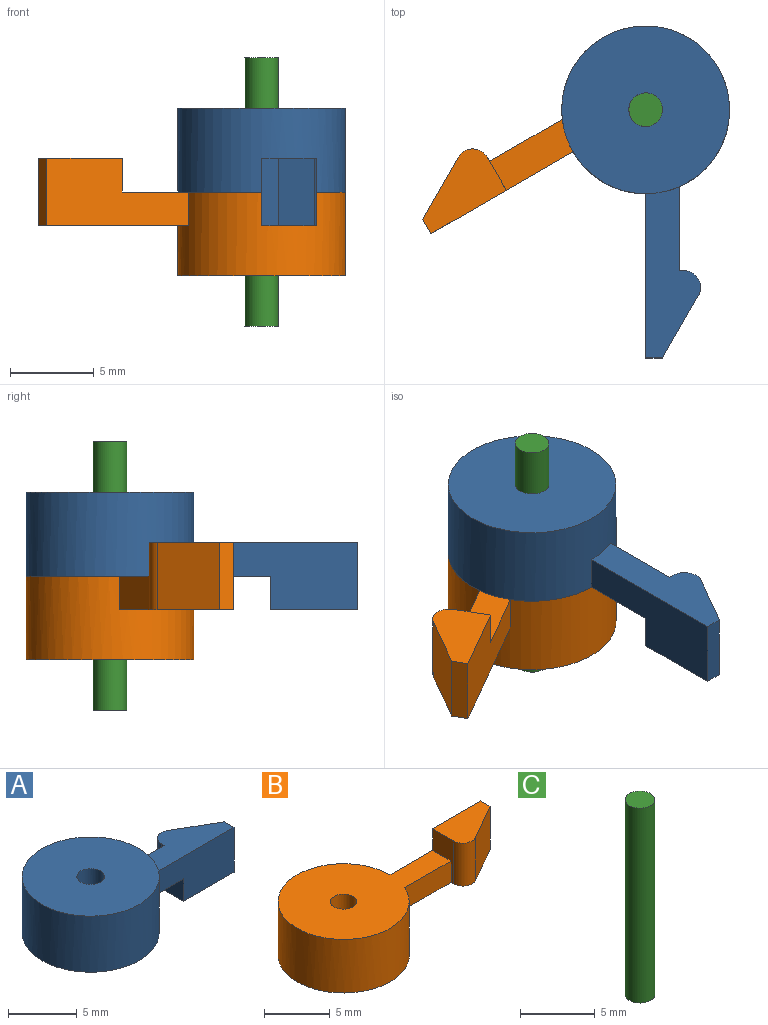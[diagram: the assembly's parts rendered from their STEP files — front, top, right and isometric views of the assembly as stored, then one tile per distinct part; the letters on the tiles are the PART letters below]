
ASSEMBLY  parts=3 mates=2
PART A: 12 faces, bbox 19.8x10x7 mm
  f0: cylinder r=5mm len=10mm, axis (0,0,-1), area 153mm2, adj f1,f2,f3,f4,f5
  f1: plane 10x10mm, normal (0,0,1), area 75.4mm2, adj f0,f10
  f2: plane 14.58x10mm, normal (0,0,-1), area 84.8mm2, adj f0,f3,f4,f6,f10
  f3: plane 9.78x4mm, normal (0,-1,0), area 29.9mm2, adj f0,f2,f5,f6,f7,f9
  f4: plane 5x2mm, normal (0,1,0), area 10mm2, adj f0,f2,f5,f6
  f5: plane 10.2x3.27mm, normal (0,0,1), area 21.7mm2, adj f0,f3,f4,f6,f7,f8,f11
  f6: plane 4x2.27mm, normal (-1,0,0), area 5.1mm2, adj f2,f3,f4,f5,f9,f11
  f7: plane 4x1mm, normal (1,0,0), area 4mm2, adj f3,f5,f8,f9
  f8: plane 4x3.7mm, normal (0.5,0.87,0), area 17.1mm2, adj f5,f7,f9,f11
  f9: plane 5.2x3.27mm, normal (0,0,-1), area 12.3mm2, adj f3,f6,f7,f8,f11
  f10: cylinder r=1mm len=5mm, axis (0,0,-1), area 31.4mm2, adj f1,f2
  f11: cylinder r=1mm len=4mm, axis (0,0,-1), area 8.4mm2, adj f5,f6,f8,f9
PART B: 12 faces, bbox 19.8x10x7 mm
  f0: cylinder r=5mm len=10mm, axis (0,0,1), area 153mm2, adj f1,f2,f3,f4,f5
  f1: plane 10x10mm, normal (0,0,-1), area 75.4mm2, adj f0,f10
  f2: plane 14.58x10mm, normal (0,0,1), area 84.8mm2, adj f0,f3,f4,f6,f10
  f3: plane 5x2mm, normal (0,-1,0), area 10mm2, adj f0,f2,f5,f6
  f4: plane 9.78x4mm, normal (0,1,0), area 29.9mm2, adj f0,f2,f5,f6,f8,f9
  f5: plane 10.2x3.27mm, normal (0,0,-1), area 21.7mm2, adj f0,f3,f4,f6,f7,f8,f11
  f6: plane 4x2.27mm, normal (-1,0,0), area 5.1mm2, adj f2,f3,f4,f5,f9,f11
  f7: plane 4x3.7mm, normal (0.5,-0.87,0), area 17.1mm2, adj f5,f8,f9,f11
  f8: plane 4x1mm, normal (1,0,0), area 4mm2, adj f4,f5,f7,f9
  f9: plane 5.2x3.27mm, normal (0,0,1), area 12.3mm2, adj f4,f6,f7,f8,f11
  f10: cylinder r=1mm len=5mm, axis (0,0,1), area 31.4mm2, adj f1,f2
  f11: cylinder r=1mm len=4mm, axis (0,0,1), area 8.4mm2, adj f5,f6,f7,f9
PART C: 3 faces, bbox 2x2x16 mm
  f0: cylinder r=1mm len=16mm, axis (0,0,-1), area 100.5mm2, adj f1,f2
  f1: plane 2x2mm, normal (0,0,1), area 3.1mm2, adj f0
  f2: plane 2x2mm, normal (0,0,-1), area 3.1mm2, adj f0
PLACE A rot(axis=(0,0,-1),90deg) t=(-16.53,-9.45,0.14)mm
PLACE B rot(axis=(0,0,-1),150deg) t=(-16.53,-9.45,0.14)mm
PLACE C t=(-16.53,-9.45,-7.86)mm fixed
MATE revolute A.f0 <-> C.f0  axis (0,0,-1) through (-16.53,-9.45,0.14)mm
MATE revolute B.f0 <-> C.f0  axis (0,0,1) through (-16.53,-9.45,0.14)mm
